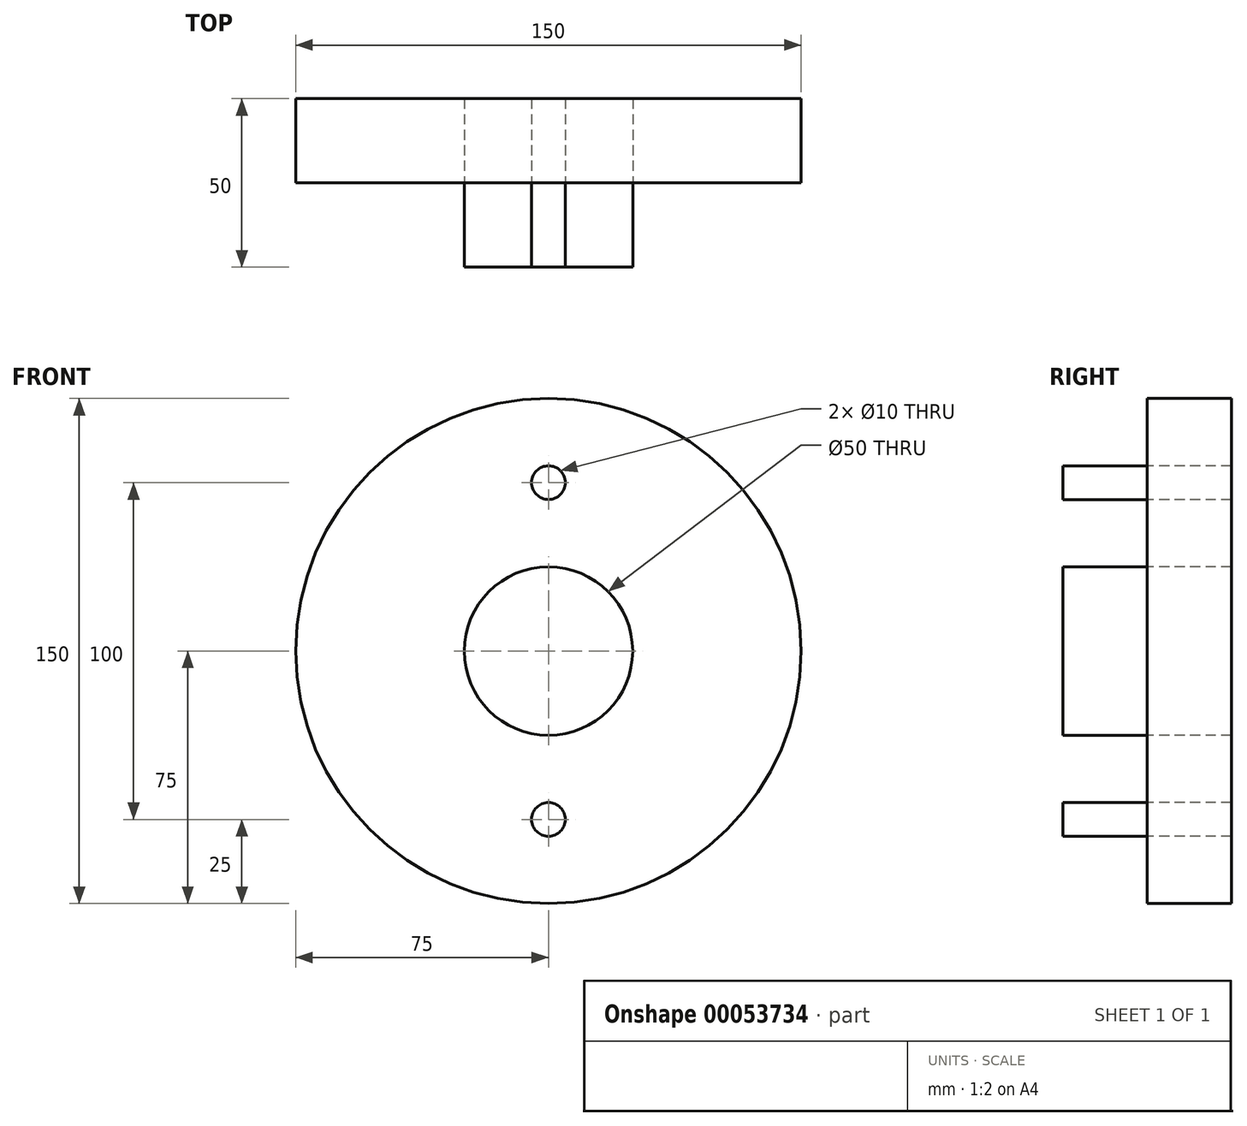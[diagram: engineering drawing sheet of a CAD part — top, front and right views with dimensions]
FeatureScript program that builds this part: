
annotation { "Feature Type Name" : "Feature", "Feature Type Description" : "" }
export const myFeature = defineFeature(function(context is Context, id is Id, definition is map)
    precondition{}
    {
        {
            var Q0;
            Q0=qCreatedBy(makeId("Front.planeOp"),FACE);
            var sketch = newSketch(context, id + "F0", { "sketchPlane" : qUnion([Q0])});
            skCircle(sketch, "E0", {"center": v(0, 0) * mm, "radius": 75 * mm});
            skCircle(sketch, "E1", {"center": v(0, 50) * mm, "radius": 5 * mm});
            skCircle(sketch, "E2", {"center": v(0, -50) * mm, "radius": 5 * mm});
            skCircle(sketch, "E3", {"center": v(0, 0) * mm, "radius": 25 * mm});
            skSolve(sketch);
        }
        {
            var Q0;
            Q0=makeQuery(id+"F0.imprint","IMPRINT",FACE,{"disambiguationData":[TD([[makeQuery(id+"F0.imprint","IMPRINT",EDGE,{"derivedFrom":sQuery(id+"F0.wireOp",EDGE,"E1")}),1.0]])]});
            var Q1;
            Q1=makeQuery(id+"F0.imprint","IMPRINT",FACE,{"disambiguationData":[TD([[makeQuery(id+"F0.imprint","IMPRINT",EDGE,{"derivedFrom":sQuery(id+"F0.wireOp",EDGE,"E3")}),1.0]])]});
            var Q2;
            Q2=makeQuery(id+"F0.imprint","IMPRINT",FACE,{"disambiguationData":[TD([[makeQuery(id+"F0.imprint","IMPRINT",EDGE,{"derivedFrom":sQuery(id+"F0.wireOp",EDGE,"E2")}),1.0]])]});
            extrude(context, id + "F1", {"entities" : qUnion([Q0, Q1, Q2]), "depth" : 25 * mm});
        }
        {
            var Q0;
            Q0=makeQuery(id+"F0.imprint","IMPRINT",FACE,{"disambiguationData":[TD([[makeQuery(id+"F0.imprint","IMPRINT",EDGE,{"derivedFrom":sQuery(id+"F0.wireOp",EDGE,"E0")}),1.0]])]});
            extrude(context, id + "F2", {"entities" : qUnion([Q0]), "oppositeDirection" : true, "depth" : 25 * mm});
        }
    });
